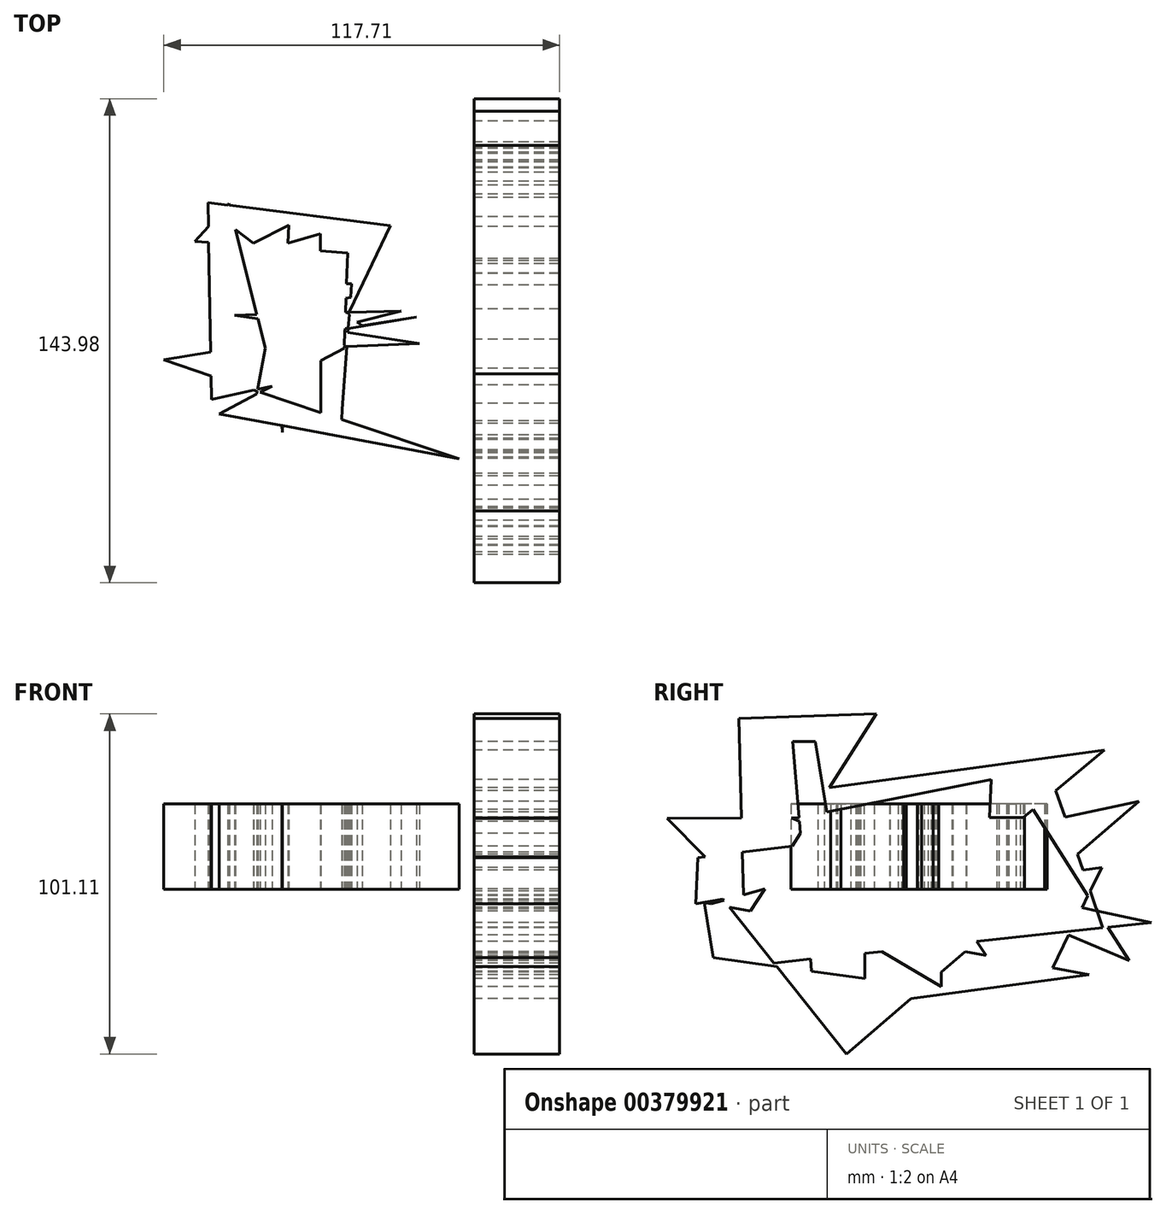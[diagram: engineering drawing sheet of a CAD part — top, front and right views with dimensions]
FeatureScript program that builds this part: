
annotation { "Feature Type Name" : "Feature", "Feature Type Description" : "" }
export const myFeature = defineFeature(function(context is Context, id is Id, definition is map)
    precondition{}
    {
        {
            var Q0;
            Q0=qCreatedBy(makeId("Right.planeOp"),FACE);
            var sketch = newSketch(context, id + "F0", { "sketchPlane" : qUnion([Q0])});
            skLineSegment(sketch, "E0", {"start": v(-50.51, 50.88) * mm, "end": v(-49.22, -1.66) * mm});
            skLineSegment(sketch, "E1", {"start": v(-57.33, 44.06) * mm, "end": v(-14.75, 44.06) * mm});
            skLineSegment(sketch, "E2", {"start": v(-28.76, 49.6) * mm, "end": v(-21.75, 6.45) * mm});
            skLineSegment(sketch, "E3", {"start": v(-34.47, 21.02) * mm, "end": v(34.66, 34.66) * mm});
            skLineSegment(sketch, "E4", {"start": v(0, 51.62) * mm, "end": v(4.24, 18.8) * mm});
            skLineSegment(sketch, "E5", {"start": v(-13.09, 8.85) * mm, "end": v(81.85, 29.13) * mm});
            skLineSegment(sketch, "E6", {"start": v(25.07, 44.61) * mm, "end": v(22.12, -15.67) * mm});
            skLineSegment(sketch, "E7", {"start": v(-40, -7.37) * mm, "end": v(83.33, 10.32) * mm});
            skLineSegment(sketch, "E8", {"start": v(-13.09, 8.85) * mm, "end": v(-13.09, -32.45) * mm});
            skLineSegment(sketch, "E9", {"start": v(-44.43, -22.3) * mm, "end": v(99.18, -7) * mm});
            skLineSegment(sketch, "E10", {"start": v(9.59, -10.7) * mm, "end": v(9.59, -36.32) * mm});
            skLineSegment(sketch, "E11", {"start": v(-26.36, -35.95) * mm, "end": v(67.1, -23.6) * mm});
            skLineSegment(sketch, "E12", {"start": v(59.92, 11.8) * mm, "end": v(34.66, -39.82) * mm});
            skLineSegment(sketch, "E13", {"start": v(33.37, 29.5) * mm, "end": v(65.63, -21.39) * mm});
            skLineSegment(sketch, "E14", {"start": v(-17.51, 38.9) * mm, "end": v(30.23, -30.05) * mm});
            skLineSegment(sketch, "E15", {"start": v(-30.6, 12.54) * mm, "end": v(99.37, -15.85) * mm});
            skLineSegment(sketch, "E16", {"start": v(68.38, 26.25) * mm, "end": v(-29.31, -58.26) * mm});
            skLineSegment(sketch, "E17", {"start": v(-60.84, -3.87) * mm, "end": v(107.85, -35.58) * mm});
            skLineSegment(sketch, "E18", {"start": v(-34.3, -41.85) * mm, "end": v(16.46, 31.07) * mm});
            skLineSegment(sketch, "E19", {"start": v(-57.52, 30.79) * mm, "end": v(70.05, -23.04) * mm});
            skLineSegment(sketch, "E20", {"start": v(-8.3, 54.38) * mm, "end": v(-56.6, -21.39) * mm});
            skLineSegment(sketch, "E21", {"start": v(-71.9, 21.2) * mm, "end": v(34.47, 21.39) * mm});
            skLineSegment(sketch, "E22", {"start": v(-35.58, 56.97) * mm, "end": v(-28.76, -26.73) * mm});
            skLineSegment(sketch, "E23", {"start": v(-64.7, 9.22) * mm, "end": v(-2.4, 16.96) * mm});
            skLineSegment(sketch, "E24", {"start": v(-58.86, -4.24) * mm, "end": v(-19.91, 6.45) * mm});
            skLineSegment(sketch, "E25", {"start": v(-56.23, -1.66) * mm, "end": v(-8.85, -61.02) * mm});
            skLineSegment(sketch, "E26", {"start": v(-60.84, -19.91) * mm, "end": v(-2.21, -28.02) * mm});
            skLineSegment(sketch, "E27", {"start": v(-60.84, -3.87) * mm, "end": v(-58, -21.39) * mm});
            skLineSegment(sketch, "E28", {"start": v(-71.9, 21.2) * mm, "end": v(-54.02, 3.13) * mm});
            skLineSegment(sketch, "E29", {"start": v(-62.71, 9.47) * mm, "end": v(-63.42, -4.24) * mm});
            skLineSegment(sketch, "E30", {"start": v(-63.42, -4.24) * mm, "end": v(-51.9, -2.33) * mm});
            skLineSegment(sketch, "E31", {"start": v(-50.51, 50.88) * mm, "end": v(6.45, 52.73) * mm});
            skLineSegment(sketch, "E32", {"start": v(8.48, 52.73) * mm, "end": v(4.24, 18.8) * mm});
            skLineSegment(sketch, "E33", {"start": v(-31.9, 29.13) * mm, "end": v(76.7, 44.06) * mm});
            skLineSegment(sketch, "E34", {"start": v(35.76, 52.73) * mm, "end": v(59.55, -16.96) * mm});
            skLineSegment(sketch, "E35", {"start": v(58.14, 41.51) * mm, "end": v(6.45, -1.66) * mm});
            skLineSegment(sketch, "E36", {"start": v(-15.85, 12.17) * mm, "end": v(76.88, 1.47) * mm});
            skLineSegment(sketch, "E37", {"start": v(14.75, 3.87) * mm, "end": v(-5.72, -23.23) * mm});
            skLineSegment(sketch, "E38", {"start": v(-32.08, -4.24) * mm, "end": v(11.25, -29.87) * mm});
            skLineSegment(sketch, "E39", {"start": v(-10.7, 11.8) * mm, "end": v(-25.07, -52.73) * mm});
            skSolve(sketch);
        }
        {
            var Q0;
            Q0 = qSketchRegion(id + "F0", true);
            extrude(context, id + "F1", {"entities" : qUnion([Q0]), "depth" : 25.4 * mm});
        }
        {
            var Q0;
            Q0=qCreatedBy(makeId("Top.planeOp"),FACE);
            var sketch = newSketch(context, id + "F2", { "sketchPlane" : qUnion([Q0])});
            skLineSegment(sketch, "E40", {"start": v(-79.46, 55.12) * mm, "end": v(-77.98, -21.57) * mm});
            skLineSegment(sketch, "E41", {"start": v(-90.15, -4.8) * mm, "end": v(7.56, 11.25) * mm});
            skLineSegment(sketch, "E42", {"start": v(-45.72, 34.66) * mm, "end": v(-45.54, -27.47) * mm});
            skLineSegment(sketch, "E43", {"start": v(-67.29, -2.4) * mm, "end": v(1.84, 14.75) * mm});
            skLineSegment(sketch, "E44", {"start": v(-37.42, 30.6) * mm, "end": v(-39.45, -24.33) * mm});
            skLineSegment(sketch, "E45", {"start": v(-78.41, 0.93) * mm, "end": v(-25.44, 9.96) * mm});
            skLineSegment(sketch, "E46", {"start": v(-56.23, 29.31) * mm, "end": v(-67.84, -32.63) * mm});
            skLineSegment(sketch, "E47", {"start": v(-39.64, 23.23) * mm, "end": v(-51.99, 16.04) * mm});
            skLineSegment(sketch, "E48", {"start": v(-70.42, 6.27) * mm, "end": v(-20.83, 16.22) * mm});
            skLineSegment(sketch, "E49", {"start": v(-35.95, 23.78) * mm, "end": v(-39.3, -20.26) * mm});
            skLineSegment(sketch, "E50", {"start": v(-69.13, -2.77) * mm, "end": v(2.4, 0) * mm});
            skLineSegment(sketch, "E51", {"start": v(-54.02, 26.36) * mm, "end": v(-21.75, -22.3) * mm});
            skLineSegment(sketch, "E52", {"start": v(-20.46, 43.7) * mm, "end": v(-42.07, -1.72) * mm});
            skLineSegment(sketch, "E53", {"start": v(-63.79, 18.07) * mm, "end": v(-5.39, 15.91) * mm});
            skLineSegment(sketch, "E54", {"start": v(-75.59, 36.69) * mm, "end": v(-31.16, 2.95) * mm});
            skLineSegment(sketch, "E55", {"start": v(-50.7, 36.69) * mm, "end": v(-89.6, 16.96) * mm});
            skLineSegment(sketch, "E56", {"start": v(-92.91, 7.19) * mm, "end": v(-21.72, 8.9) * mm});
            skLineSegment(sketch, "E57", {"start": v(-59.73, 42.03) * mm, "end": v(-56.88, -31.71) * mm});
            skLineSegment(sketch, "E58", {"start": v(-99.37, -6.82) * mm, "end": v(11.23, 12.03) * mm});
            skLineSegment(sketch, "E59", {"start": v(-55.18, 34.41) * mm, "end": v(-57.06, -27.13) * mm});
            skLineSegment(sketch, "E60", {"start": v(-92, 10.88) * mm, "end": v(-7.74, -2.03) * mm});
            skLineSegment(sketch, "E61", {"start": v(-73, 41.3) * mm, "end": v(-62.04, -2.5) * mm});
            skPoint(sketch, "E61.endSnap0", {"position": v(-62.04, -1.66) * mm});
            skLineSegment(sketch, "E62", {"start": v(-90.89, 30.23) * mm, "end": v(-20.3, 24.86) * mm});
            skLineSegment(sketch, "E63", {"start": v(-86.1, 42.03) * mm, "end": v(-7, 32.08) * mm});
            skLineSegment(sketch, "E64", {"start": v(-64.34, 50.33) * mm, "end": v(-94.2, 17.33) * mm});
            skLineSegment(sketch, "E65", {"start": v(-97.52, -3.87) * mm, "end": v(-4.42, -35.03) * mm});
            skLineSegment(sketch, "E66", {"start": v(-4.42, -35.03) * mm, "end": v(-75.86, -21.63) * mm});
            skLineSegment(sketch, "E67", {"start": v(-75.86, -21.63) * mm, "end": v(-37.9, -1.72) * mm});
            skLineSegment(sketch, "E68", {"start": v(-37.9, -1.72) * mm, "end": v(-78.83, 22.42) * mm});
            skLineSegment(sketch, "E69", {"start": v(-78.83, 22.42) * mm, "end": v(-33.37, 35.4) * mm});
            skLineSegment(sketch, "E70", {"start": v(-84.62, -18.8) * mm, "end": v(-43.88, -9.77) * mm});
            skSolve(sketch);
        }
        {
            var Q0;
            Q0 = qSketchRegion(id + "F2", true);
            extrude(context, id + "F3", {"entities" : qUnion([Q0]), "depth" : 25.4 * mm});
        }
    });
